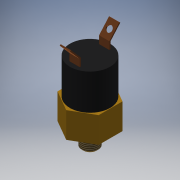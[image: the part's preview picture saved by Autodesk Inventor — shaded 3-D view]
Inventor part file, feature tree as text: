
AUTODESK INVENTOR PART (.ipt)
format: ipt  version: 2017.1 (Build 211199000, 199)  size: 180,736 bytes
history: native  units: mm (DEFAULTED — no unit token found)
features: extrude x6, sketch x6, projected_geometry x4, mirror x1, thread x1, chamfer x1, fillet x1
ambient origin geometry x8: Origin, YZ Plane, XZ Plane, XY Plane, X Axis, Y Axis, Z Axis, Center Point
bodies: Solid1 (feature_tree)
feature tree (20):
  extrude  "Extrusion1"  Depth=15.875mm TaperAngle=0.0deg
  extrude  "Extrusion2"  Depth=11.049mm TaperAngle=0.0deg
  extrude  "Extrusion3"  Depth=19.9898mm TaperAngle=0.0deg
  extrude  "Extrusion4"  Depth=21.971mm TaperAngle=0.0deg
  extrude  "Extrusion5"  Depth=0.762mm
  extrude  "Extrusion6"  Depth=3.175mm
  mirror  "Mirror1"
  thread  "Thread1"  [1 undecoded]
  chamfer  "Chamfer1"  Distance=6.35mm
  fillet  "Fillet1"  Radius=6.35mm
  sketch  "Sketch1"  dims[d0=25.4mm d1=15.875mm d2=0.0mm]
  sketch  "Sketch2"  dims[d3=10.16mm d4=11.049mm d5=0.0mm]
  projected_geometry  "Projected Loop1"
  sketch  "Sketch3"  dims[d6=3.175mm d7=19.9898mm d8=0.0mm]
  sketch  "Sketch4"  dims[d9=24.765mm d10=21.971mm d11=0.0mm]
  projected_geometry  "Projected Loop2"
  sketch  "Sketch5"  dims[d12=19.05mm d13=0.762mm]
  projected_geometry  "Projected Loop3"
  sketch  "Sketch6"  dims[d14=0.762mm d15=4.699mm d17=9.398mm d18=6.35mm d19=0.0mm d20=6.35mm d21=0.0mm d22=25.4mm d23=0.0mm d24=1.0mm d25=3.175mm d26=45.0deg d27=3.175mm]
  projected_geometry  "Projected Loop4"
note: 1 required parameter value undecoded (feature->parameter linkage not recoverable at this tier; creation-order binding heuristic only, values carry confidence <= 0.55)
